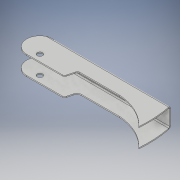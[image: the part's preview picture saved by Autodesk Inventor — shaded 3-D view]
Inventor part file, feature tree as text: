
AUTODESK INVENTOR PART (.ipt)
format: ipt  version: 2019 (Build 230136000, 136)  size: 228,352 bytes
history: native  units: mm
features: sheet_metal_op x3, sketch x3, other x1
ambient origin geometry x8: Origin, YZ Plane, XZ Plane, XY Plane, X Axis, Y Axis, Z Axis, Center Point
bodies: Solid1 (feature_tree)
feature tree (7):
  sheet_metal_op  "Face1"
  sheet_metal_op  "Fold1"
  sheet_metal_op  "Fold2"
  sketch  "Sketch1"  dims[d1=32.0mm]
  other  "Plate1"
  sketch  "Sketch2"  dims[d2=12.0mm]
  sketch  "Sketch3"  dims[d3=12.0mm d6=15.0deg d7=15.0deg d8=17.0mm d9=17.0mm d10=12.0mm d11=8.0mm d12=105.0deg d13=105.0deg d14=19.0mm d15=22.0mm d16=2.0mm d17=1.0mm d18=1.0mm d19=2.5mm d20=2.5mm d21=3.0mm d22=3.0mm d23=9.0mm d24=9.0mm d25=38.0mm d26=54.0mm d27=2.5mm d28=28.0mm d29=25.0mm d30=8.0mm d31=15.0mm d32=50.0mm d33=50.0mm d34=25.0mm d35=25.0mm d36=0.5mm d37=0.5mm d38=0.25mm d39=1.0mm d40=0.5mm d41=90.0deg d42=0.5mm d43=0.5mm d44=0.25mm d45=1.0mm d46=0.5mm d47=90.0deg d48=0.5mm]
